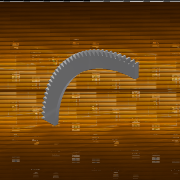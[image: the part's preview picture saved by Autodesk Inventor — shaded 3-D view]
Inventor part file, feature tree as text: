
AUTODESK INVENTOR PART (.ipt)
format: ipt  version: 2017 (Build 210142000, 142)  size: 497,664 bytes
history: native  units: mm (DEFAULTED — no unit token found)
features: sketch x4, extrude x3, plane x3, other x3
ambient origin geometry x8: Origin, YZ Plane, XZ Plane, XY Plane, X Axis, Y Axis, Z Axis, Center Point
bodies: Solid1 (feature_tree)
feature tree (13):
  extrude  "Extrusion1"  Depth=6.35mm TaperAngle=0.0deg
  plane  "Work Plane1"
  plane  "Work Plane2"
  plane  "Work Plane3"
  other  "Spur Gear"
  extrude  "Extrusion2"  Depth=76.2mm TaperAngle=0.0deg
  extrude  "Extrusion3"  TaperAngle=0.0deg  [1 undecoded]
  sketch  "Sketch1"  dims[d0=330.2mm d1=6.35mm d2=0.0mm]
  sketch  "Sketch2"  dims[d3=325.12mm d4=76.2mm d5=0.0mm]
  other  "Srf1"
  sketch  "Sketch3"  dims[d6=0.0mm d7=0.245437mm d9=0.0mm]
  sketch  "Sketch4"  dims[d14=0.0mm d15=181.61mm d16=0.0mm d17=0.0mm d18=0.0mm d19=181.61mm d20=282.575mm d21=25.4mm d22=0.0mm d23=0.0mm d24=0.0mm]
  other  "Pitch Diameter"
note: 1 required parameter value undecoded (feature->parameter linkage not recoverable at this tier; creation-order binding heuristic only, values carry confidence <= 0.55)
